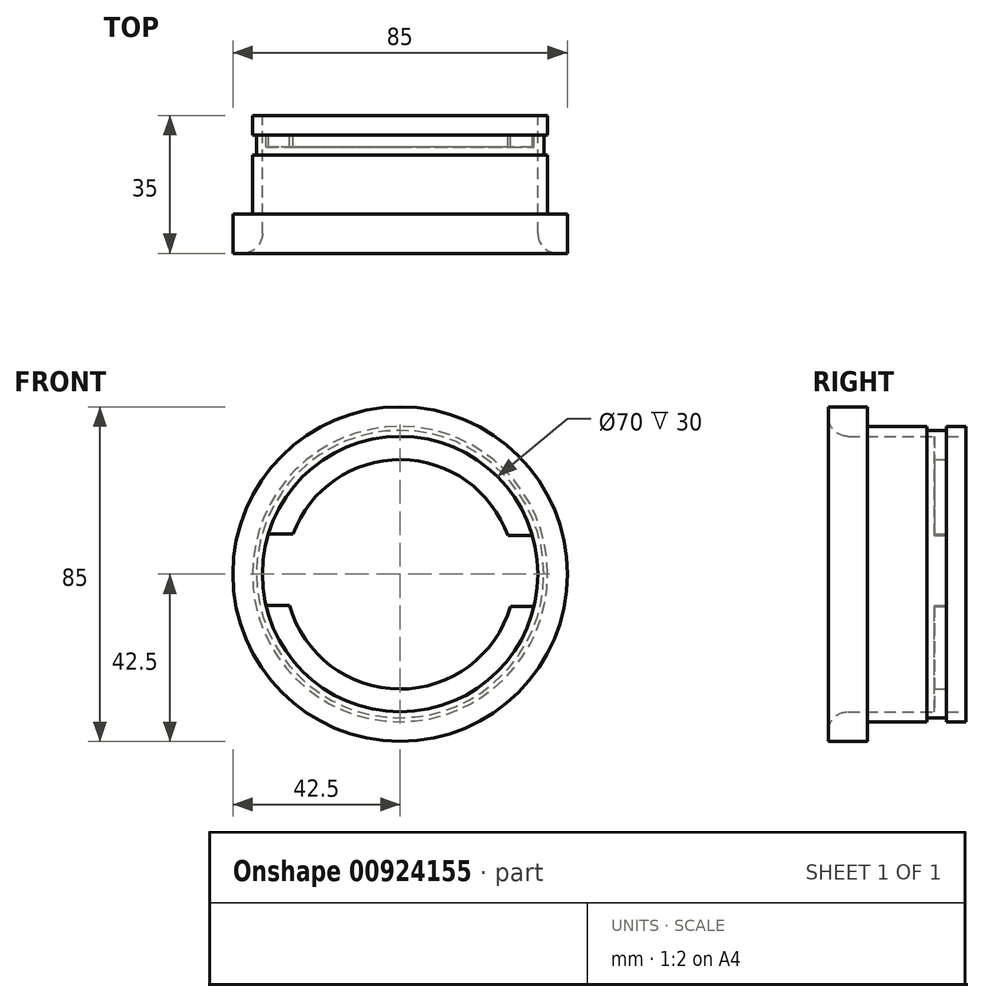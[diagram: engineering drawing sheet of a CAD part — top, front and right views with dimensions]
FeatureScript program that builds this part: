
annotation { "Feature Type Name" : "Feature", "Feature Type Description" : "" }
export const myFeature = defineFeature(function(context is Context, id is Id, definition is map)
    precondition{}
    {
        {
            var Q0;
            Q0=qCreatedBy(makeId("Front.planeOp"),FACE);
            var sketch = newSketch(context, id + "F0", { "sketchPlane" : qUnion([Q0])});
            skCircle(sketch, "E0", {"center": v(0, 0) * mm, "radius": 35 * mm});
            skCircle(sketch, "E1", {"center": v(0, 0) * mm, "radius": 37.5 * mm});
            skSolve(sketch);
        }
        {
            var Q0;
            Q0=makeQuery(id+"F0.imprint","IMPRINT",FACE,{"disambiguationData":[TD([[makeQuery(id+"F0.imprint","IMPRINT",EDGE,{"derivedFrom":sQuery(id+"F0.wireOp",EDGE,"E0")}),-1.0]])]});
            extrude(context, id + "F1", {"entities" : qUnion([Q0]), "depth" : 25 * mm, "offsetDistance" : 25 * mm});
        }
        {
            var Q0;
            Q0=makeQuery(id+"F1.opExtrude","CAP_FACE",FACE,{"disambiguationData":[OSD([sQuery(id+"F0.wireOp",EDGE,"E0"),sQuery(id+"F0.wireOp",EDGE,"E1")])],"isStart":false});
            var sketch = newSketch(context, id + "F2", { "sketchPlane" : qUnion([Q0])});
            skCircle(sketch, "E2", {"center": v(0, 0) * mm, "radius": 42.5 * mm});
            skCircle(sketch, "E3", {"center": v(0, 0) * mm, "radius": 35 * mm});
            skSolve(sketch);
        }
        {
            var Q0;
            Q0 = qSketchRegion(id + "F2", true);
            extrude(context, id + "F3", {"entities" : qUnion([Q0]), "operationType" : NewBodyOperationType.ADD, "depth" : 10 * mm, "offsetDistance" : 25 * mm});
        }
        {
            var Q0;
            Q0=makeQuery(id+"F3.opExtrude","CAP_EDGE",EDGE,{"disambiguationData":[OSD([sQuery(id+"F2.wireOp",EDGE,"E3")])],"isStart":false});
            fillet(context, id + "F4", {"entities" : qUnion([Q0]), "radius" : 5 * mm, "tangentPropagation" : true, "allowEdgeOverflow" : false});
        }
        {
            var Q0;
            Q0=qCreatedBy(makeId("Front.planeOp"),FACE);
            cPlane(context, id + "F5", {"entities" : qUnion([Q0]), "cplaneType" : CPlaneType.OFFSET, "offset" : 5 * mm, "width" : 150 * mm, "height" : 150 * mm});
        }
        {
            var Q0;
            Q0=qCreatedBy(id+"F5.planeOp",FACE);
            var sketch = newSketch(context, id + "F6", { "sketchPlane" : qUnion([Q0])});
            skCircle(sketch, "E4", {"center": v(0, 0) * mm, "radius": 37.5 * mm});
            skCircle(sketch, "E5", {"center": v(0, 0) * mm, "radius": 36.5 * mm});
            skSolve(sketch);
        }
        {
            var Q0;
            Q0 = qSketchRegion(id + "F6", true);
            extrude(context, id + "F7", {"entities" : qUnion([Q0]), "operationType" : NewBodyOperationType.REMOVE, "depth" : 5 * mm, "offsetDistance" : 25 * mm});
        }
        {
            var Q0;
            Q0=qCreatedBy(id+"F5.planeOp",FACE);
            var sketch = newSketch(context, id + "F8", { "sketchPlane" : qUnion([Q0])});
            skArc(sketch, "E6", {"start": v(33.61, 9.75) * mm, "mid": v(0.23, 35) * mm, "end": v(-33.49, 10.19) * mm});
            skArc(sketch, "E7", {"start": v(27.4, 9.75) * mm, "mid": v(0.23, 29.08) * mm, "end": v(-27.24, 10.19) * mm});
            skLineSegment(sketch, "E8", {"start": v(33.61, 9.75) * mm, "end": v(27.4, 9.75) * mm});
            skLineSegment(sketch, "E9", {"start": v(-27.24, 10.19) * mm, "end": v(-33.49, 10.19) * mm});
            skSolve(sketch);
        }
        {
            var Q0;
            Q0=makeQuery(id+"F8.imprint","IMPRINT",FACE,{"disambiguationData":[TD([[makeQuery(id+"F8.imprint","IMPRINT",EDGE,{"derivedFrom":sQuery(id+"F8.wireOp",EDGE,"E6")}),1.0]])]});
            extrude(context, id + "F9", {"entities" : qUnion([Q0]), "operationType" : NewBodyOperationType.ADD, "depth" : 3 * mm, "offsetDistance" : 25 * mm});
        }
        {
            var Q0;
            Q0=qCreatedBy(id+"F5.planeOp",FACE);
            var sketch = newSketch(context, id + "F10", { "sketchPlane" : qUnion([Q0])});
            skArc(sketch, "E10", {"start": v(-34.08, -7.97) * mm, "mid": v(-0.1, -35) * mm, "end": v(34.03, -8.18) * mm});
            skArc(sketch, "E11", {"start": v(-28.11, -7.97) * mm, "mid": v(-0.1, -29.22) * mm, "end": v(28.05, -8.18) * mm});
            skLineSegment(sketch, "E12", {"start": v(-34.08, -7.97) * mm, "end": v(-28.11, -7.97) * mm});
            skLineSegment(sketch, "E13", {"start": v(28.05, -8.18) * mm, "end": v(34.03, -8.18) * mm});
            skSolve(sketch);
        }
        {
            var Q0;
            Q0=makeQuery(id+"F10.imprint","IMPRINT",FACE,{"disambiguationData":[TD([[makeQuery(id+"F10.imprint","IMPRINT",EDGE,{"derivedFrom":sQuery(id+"F10.wireOp",EDGE,"E10")}),1.0]])]});
            extrude(context, id + "F11", {"entities" : qUnion([Q0]), "operationType" : NewBodyOperationType.ADD, "depth" : 3 * mm, "offsetDistance" : 25 * mm});
        }
    });
